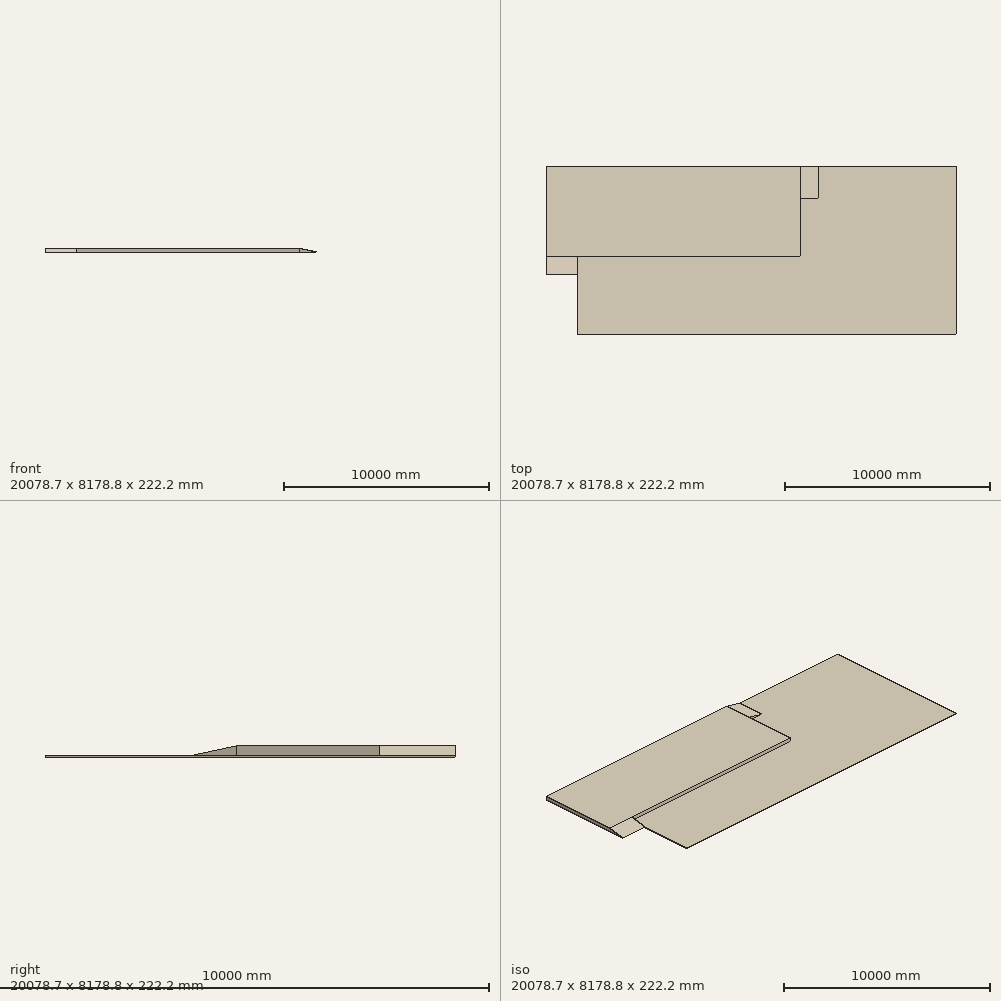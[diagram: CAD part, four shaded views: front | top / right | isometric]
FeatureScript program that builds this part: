
annotation { "Feature Type Name" : "Feature", "Feature Type Description" : "" }
export const myFeature = defineFeature(function(context is Context, id is Id, definition is map)
    precondition{}
    {
        {
            var Q0;
            Q0=qCreatedBy(makeId("Top.planeOp"),FACE);
            var sketch = newSketch(context, id + "F0", { "sketchPlane" : qUnion([Q0])});
            skLineSegment(sketch, "E0.bottom", {"start": v(0, 0) * mm, "end": v(10896.6, 0) * mm});
            skLineSegment(sketch, "E0.top", {"start": v(0, -3810) * mm, "end": v(10896.6, -3810) * mm});
            skLineSegment(sketch, "E0.left", {"start": v(0, 0) * mm, "end": v(0, -3810) * mm});
            skLineSegment(sketch, "E0.right", {"start": v(10896.6, 0) * mm, "end": v(10896.6, -3810) * mm});
            skLineSegment(sketch, "E1", {"start": v(10896.6, 0) * mm, "end": v(10896.6, 2844.8) * mm});
            skLineSegment(sketch, "E2", {"start": v(10896.6, 2844.8) * mm, "end": v(11811, 2844.8) * mm});
            skLineSegment(sketch, "E3", {"start": v(11811, 2844.8) * mm, "end": v(11811, 4368.8) * mm});
            skLineSegment(sketch, "E4", {"start": v(11811, 4368.8) * mm, "end": v(10896.6, 4368.8) * mm});
            skLineSegment(sketch, "E5", {"start": v(10896.6, 4368.8) * mm, "end": v(0, 4368.8) * mm});
            skLineSegment(sketch, "E6", {"start": v(11811, 4368.8) * mm, "end": v(18554.7, 4368.8) * mm});
            skLineSegment(sketch, "E7", {"start": v(18554.7, 4368.8) * mm, "end": v(18554.7, -3810) * mm});
            skLineSegment(sketch, "E8", {"start": v(18554.7, -3810) * mm, "end": v(10896.6, -3810) * mm});
            skLineSegment(sketch, "E9", {"start": v(0, -914.4) * mm, "end": v(-1524, -914.4) * mm});
            skLineSegment(sketch, "E10", {"start": v(-1524, -914.4) * mm, "end": v(-1524, 4368.8) * mm});
            skLineSegment(sketch, "E11", {"start": v(-1524, 4368.8) * mm, "end": v(0, 4368.8) * mm});
            skSolve(sketch);
        }
        {
            var Q0;
            Q0=makeQuery(id+"F0.imprint","IMPRINT",FACE,{"disambiguationData":[TD([[makeQuery(id+"F0.imprint","IMPRINT",EDGE,{"derivedFrom":sQuery(id+"F0.wireOp",EDGE,"E0.bottom")}),-1.0]])]});
            extrude(context, id + "F1", {"entities" : qUnion([Q0]), "oppositeDirection" : true, "depth" : 25.4 * mm});
        }
        {
            var Q0;
            Q0=makeQuery(id+"F0.imprint","IMPRINT",FACE,{"disambiguationData":[TD([[makeQuery(id+"F0.imprint","IMPRINT",EDGE,{"derivedFrom":sQuery(id+"F0.wireOp",EDGE,"E0.bottom")}),1.0]])]});
            extrude(context, id + "F2", {"entities" : qUnion([Q0]), "operationType" : NewBodyOperationType.ADD, "depth" : 196.85 * mm});
        }
        {
            var Q0;
            Q0=makeQuery(id+"F2.opExtrude","SWEPT_FACE",FACE,{"disambiguationData":[OSD([sQuery(id+"F0.wireOp",EDGE,"E2")])]});
            var sketch = newSketch(context, id + "F3", { "sketchPlane" : qUnion([Q0])});
            skLineSegment(sketch, "E12", {"start": v(11811, 0) * mm, "end": v(10896.6, 196.85) * mm});
            skLineSegment(sketch, "E13", {"start": v(10896.6, 196.85) * mm, "end": v(11811, 196.85) * mm});
            skLineSegment(sketch, "E14", {"start": v(11811, 196.85) * mm, "end": v(11811, 0) * mm});
            skSolve(sketch);
        }
        {
            var Q0;
            Q0=makeQuery(id+"F3.imprint","IMPRINT",FACE,{"disambiguationData":[TD([[makeQuery(id+"F3.imprint","IMPRINT",EDGE,{"derivedFrom":sQuery(id+"F3.wireOp",EDGE,"E12")}),-1.0]])]});
            var Q1;
            Q1=makeQuery(id+"F2.opExtrude","SWEPT_FACE",FACE,{"disambiguationData":[OSD([sQuery(id+"F0.wireOp",EDGE,"E4"),sQuery(id+"F0.wireOp",EDGE,"E5")])]});
            extrude(context, id + "F4", {"entities" : qUnion([Q0]), "operationType" : NewBodyOperationType.REMOVE, "endBound" : BoundingType.UP_TO_SURFACE, "oppositeDirection" : true, "endBoundEntityFace" : qUnion([Q1]), "depth" : 25.4 * mm});
        }
        {
            var Q0;
            Q0=makeQuery(id+"F0.imprint","IMPRINT",FACE,{"disambiguationData":[TD([[makeQuery(id+"F0.imprint","IMPRINT",EDGE,{"derivedFrom":sQuery(id+"F0.wireOp",EDGE,"E0.right")}),1.0]])]});
            extrude(context, id + "F5", {"entities" : qUnion([Q0]), "operationType" : NewBodyOperationType.ADD, "oppositeDirection" : true, "depth" : 25.4 * mm});
        }
        {
            var Q0;
            Q0=makeQuery(id+"F2.opExtrude","SWEPT_FACE",FACE,{"disambiguationData":[OSD([sQuery(id+"F0.wireOp",EDGE,"E0.left")])]});
            var sketch = newSketch(context, id + "F6", { "sketchPlane" : qUnion([Q0])});
            skLineSegment(sketch, "E15", {"start": v(-914.4, 0) * mm, "end": v(0, 196.85) * mm});
            skLineSegment(sketch, "E16", {"start": v(0, 196.85) * mm, "end": v(-914.4, 196.85) * mm});
            skLineSegment(sketch, "E17", {"start": v(-914.4, 196.85) * mm, "end": v(-914.4, 0) * mm});
            skSolve(sketch);
        }
        {
            var Q0;
            Q0=makeQuery(id+"F6.imprint","IMPRINT",FACE,{"disambiguationData":[TD([[makeQuery(id+"F6.imprint","IMPRINT",EDGE,{"derivedFrom":sQuery(id+"F6.wireOp",EDGE,"E15")}),1.0]])]});
            var Q1;
            Q1=makeQuery(id+"F2.opExtrude","SWEPT_FACE",FACE,{"disambiguationData":[OSD([sQuery(id+"F0.wireOp",EDGE,"E10")])]});
            extrude(context, id + "F7", {"entities" : qUnion([Q0]), "operationType" : NewBodyOperationType.REMOVE, "endBound" : BoundingType.UP_TO_SURFACE, "oppositeDirection" : true, "endBoundEntityFace" : qUnion([Q1]), "depth" : 25.4 * mm});
        }
    });
